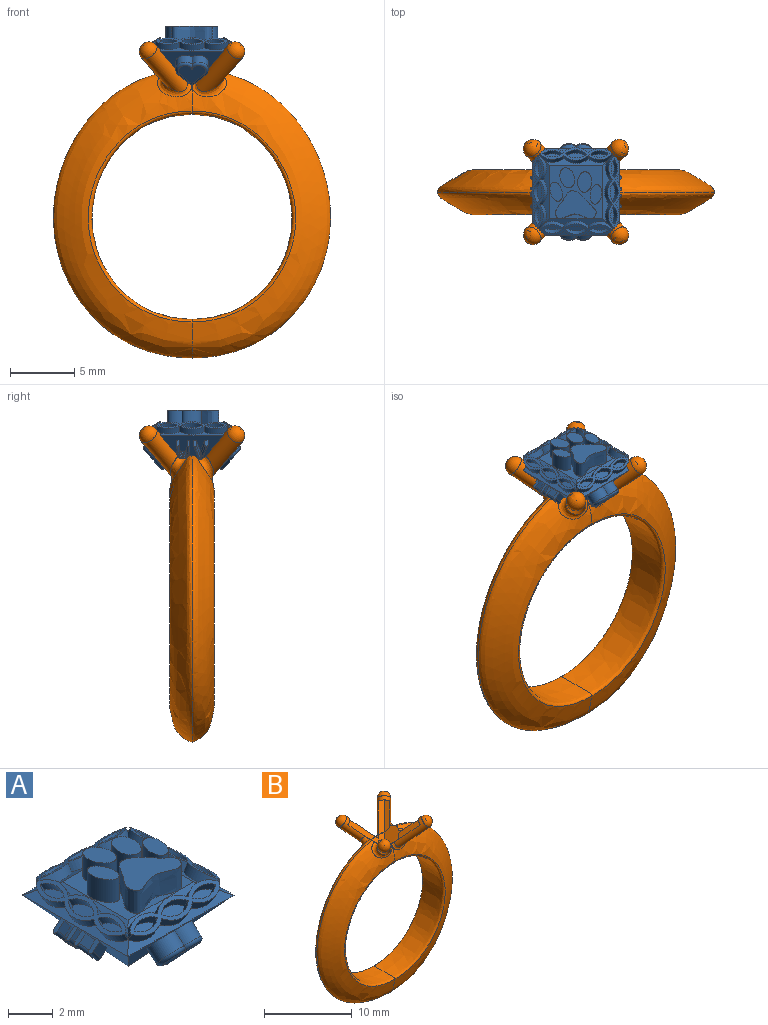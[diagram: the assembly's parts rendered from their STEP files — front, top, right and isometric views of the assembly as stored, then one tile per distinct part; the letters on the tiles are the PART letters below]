
ASSEMBLY  parts=2 mates=1
PART A: 238 faces, bbox 7.4x7.8x6 mm
  f0: plane 6.71x3.89mm, normal (0.76,0,-0.65), area 16mm2, adj f1,f54,f57,f114,f115,f116,f117,f118
  f1: plane 6.71x3.89mm, normal (0,-0.76,-0.65), area 13.2mm2, adj f0,f37,f52,f104,f105,f106,f107
  f2: plane 2.31x0.42mm, normal (0,0,1), area 0.5mm2, adj f35,f94
  f3: plane 4.19x4.17mm, normal (0,0,1), area 7.6mm2, adj f5,f16,f35,f51,f94,f96,f98,f100
  f4: cylinder r=0.1mm len=0.48mm, axis (0.5,0,-0.87), area 0mm2, adj f8,f9,f22,f65,f89
  f5: plane 4.83x0.53mm, normal (-0.5,0,0.87), area 1.4mm2, adj f3,f10,f12,f16,f35,f89,f90
  f6: plane 1.49x0.5mm, normal (-0.5,0,0.87), area 0.6mm2, adj f23,f87
  f7: plane 6.71x0.57mm, normal (-0.5,0,0.87), area 2.3mm2, adj f9,f11,f18,f37,f48,f52,f92
  f8: cylinder r=0.1mm len=0.47mm, axis (0,-0.5,-0.87), area 0mm2, adj f4,f14,f22,f63,f89
  f9: cylinder r=1.3mm len=1.84mm, axis (0.5,0,-0.87), area 1mm2, adj f4,f7,f22,f48,f65,f92
  f10: cylinder r=1.3mm len=1.91mm, axis (0.5,0,-0.87), area 1.1mm2, adj f5,f65,f89,f90
  f11: cylinder r=1.3mm len=1.84mm, axis (0.5,0,-0.87), area 1mm2, adj f7,f40,f41,f42,f46,f65,f92
  f12: plane 0.02x0.02mm, normal (0,0.5,-0.87), area 0mm2, adj f5,f13,f90
  f13: cylinder r=1.3mm len=1.84mm, axis (0,0.5,-0.87), area 0.9mm2, adj f12,f35,f40,f42,f43,f70,f90
  f14: cylinder r=1.3mm len=1.84mm, axis (0,-0.5,-0.87), area 0.9mm2, adj f8,f16,f21,f63,f88,f89
  f15: cylinder r=0.1mm len=0.48mm, axis (0,-0.5,-0.87), area 0mm2, adj f19,f20,f31,f63,f83
  f16: plane 4.83x0.53mm, normal (0,0.5,0.87), area 1.4mm2, adj f3,f5,f14,f21,f51,f83,f88
  f17: plane 1.49x0.5mm, normal (0,0.5,0.87), area 0.6mm2, adj f32,f81
  f18: plane 6.71x0.57mm, normal (0,0.5,0.87), area 2.3mm2, adj f7,f20,f22,f50,f54,f57,f85
  f19: cylinder r=0.1mm len=0.47mm, axis (-0.5,0,-0.87), area 0mm2, adj f15,f24,f31,f60,f83
  f20: cylinder r=1.3mm len=1.84mm, axis (0,-0.5,-0.87), area 1mm2, adj f15,f18,f31,f50,f63,f85
  f21: cylinder r=1.3mm len=1.91mm, axis (0,-0.5,-0.87), area 1.1mm2, adj f14,f16,f63,f83
  f22: cylinder r=1.3mm len=1.84mm, axis (0,-0.5,-0.87), area 1mm2, adj f4,f8,f9,f18,f48,f63,f85
  f23: cylinder r=1.1mm len=1.49mm, axis (0.5,0,-0.87), area 0.8mm2, adj f6,f65,f87
  f24: cylinder r=1.3mm len=1.84mm, axis (-0.5,0,-0.87), area 0.9mm2, adj f19,f30,f51,f60,f82,f83
  f25: cylinder r=0.1mm len=0.48mm, axis (-0.5,0,-0.87), area 0mm2, adj f26,f33,f44,f60,f77
  f26: cylinder r=1.3mm len=1.84mm, axis (-0.5,0,-0.87), area 1mm2, adj f25,f44,f54,f60,f66,f79
  f27: plane 1.49x0.5mm, normal (0.5,0,0.87), area 0.6mm2, adj f38,f75
  f28: plane 1.49x0.5mm, normal (0.5,0,0.87), area 0.6mm2, adj f58,f78
  f29: plane 1.64x0.63mm, normal (0.5,0,0.87), area 0.8mm2, adj f59,f80
  f30: cylinder r=1.3mm len=1.91mm, axis (-0.5,0,-0.87), area 1.1mm2, adj f24,f51,f60,f77
  f31: cylinder r=1.3mm len=1.84mm, axis (-0.5,0,-0.87), area 1mm2, adj f15,f19,f20,f50,f54,f60,f79
  f32: cylinder r=1.1mm len=1.49mm, axis (0,-0.5,-0.87), area 0.8mm2, adj f17,f63,f81
  f33: cylinder r=0.1mm len=0.47mm, axis (0,0.5,-0.87), area 0mm2, adj f25,f34,f44,f70,f77
  f34: cylinder r=1.3mm len=1.84mm, axis (0,0.5,-0.87), area 0.9mm2, adj f33,f35,f43,f70,f76,f77
  f35: plane 4.84x0.54mm, normal (0,-0.5,0.87), area 1.4mm2, adj f2,f3,f5,f13,f34,f43,f51,f76
  f36: plane 1.49x0.5mm, normal (0,-0.5,0.87), area 0.6mm2, adj f68,f74
  f37: plane 6.71x0.57mm, normal (0,-0.5,0.87), area 2.3mm2, adj f1,f7,f41,f44,f46,f54,f72
  f38: cylinder r=1.1mm len=1.49mm, axis (-0.5,0,-0.87), area 0.8mm2, adj f27,f60,f75
  f39: cylinder r=1.1mm len=1.49mm, axis (0.5,0,-0.87), area 0.8mm2, adj f47,f65,f91
  f40: cylinder r=0.1mm len=0.47mm, axis (0.5,0,-0.87), area 0mm2, adj f11,f13,f42,f65,f90
  f41: cylinder r=1.3mm len=1.84mm, axis (0,0.5,-0.87), area 1mm2, adj f11,f37,f42,f46,f70,f72
  f42: cylinder r=0.1mm len=0.48mm, axis (0,0.5,-0.87), area 0mm2, adj f11,f13,f40,f41,f70
  f43: cylinder r=1.3mm len=1.91mm, axis (0,0.5,-0.87), area 1.1mm2, adj f13,f34,f35,f70
  f44: cylinder r=1.3mm len=1.84mm, axis (0,0.5,-0.87), area 1mm2, adj f25,f26,f33,f37,f66,f70,f72
  f45: plane 1.49x0.5mm, normal (0,-0.5,0.87), area 0.6mm2, adj f67,f71
  f46: plane 0x0mm, normal (0.5,0,-0.87), area 0mm2, adj f11,f37,f41
  f47: plane 1.49x0.5mm, normal (-0.5,0,0.87), area 0.6mm2, adj f39,f91
  f48: plane 0x0mm, normal (0,-0.5,-0.87), area 0mm2, adj f7,f9,f22
  f49: plane 1.49x0.5mm, normal (0,0.5,0.87), area 0.6mm2, adj f61,f84
  f50: plane 0x0mm, normal (-0.5,0,-0.87), area 0mm2, adj f18,f20,f31
  f51: plane 4.83x0.53mm, normal (0.5,0,0.87), area 1.4mm2, adj f3,f16,f24,f30,f35,f77,f82
  f52: plane 6.71x3.89mm, normal (-0.76,0,-0.65), area 16mm2, adj f1,f7,f57,f148,f149,f150,f151,f152
  f53: plane 1.64x0.63mm, normal (-0.5,0,0.87), area 0.8mm2, adj f64,f93
  f54: plane 6.71x0.57mm, normal (0.5,0,0.87), area 2.3mm2, adj f0,f18,f26,f31,f37,f66,f79
  f55: plane 1.64x0.63mm, normal (0,0.5,0.87), area 0.8mm2, adj f62,f86
  f56: plane 1.64x0.63mm, normal (0,-0.5,0.87), area 0.8mm2, adj f69,f73
  f57: plane 6.71x3.89mm, normal (0,0.76,-0.65), area 13.2mm2, adj f0,f18,f52,f109,f110,f111,f112
  f58: cylinder r=1.1mm len=1.49mm, axis (-0.5,0,-0.87), area 0.8mm2, adj f28,f60,f78
  f59: cylinder r=1.1mm len=1.64mm, axis (-0.5,0,-0.87), area 0.9mm2, adj f29,f60,f80
  f60: plane 5.64x0.98mm, normal (0.5,0,0.87), area 2.4mm2, adj f19,f24,f25,f26,f30,f31,f38,f58
  f61: cylinder r=1.1mm len=1.49mm, axis (0,-0.5,-0.87), area 0.8mm2, adj f49,f63,f84
  f62: cylinder r=1.1mm len=1.64mm, axis (0,-0.5,-0.87), area 0.9mm2, adj f55,f63,f86
  f63: plane 5.64x0.98mm, normal (0,0.5,0.87), area 2.4mm2, adj f8,f14,f15,f20,f21,f22,f32,f61
  f64: cylinder r=1.1mm len=1.64mm, axis (0.5,0,-0.87), area 0.9mm2, adj f53,f65,f93
  f65: plane 5.64x0.98mm, normal (-0.5,0,0.87), area 2.4mm2, adj f4,f9,f10,f11,f23,f39,f40,f64
  f66: plane 0x0mm, normal (0,0.5,-0.87), area 0mm2, adj f26,f44,f54
  f67: cylinder r=1.1mm len=1.49mm, axis (0,0.5,-0.87), area 0.8mm2, adj f45,f70,f71
  f68: cylinder r=1.1mm len=1.49mm, axis (0,0.5,-0.87), area 0.8mm2, adj f36,f70,f74
  f69: cylinder r=1.1mm len=1.64mm, axis (0,0.5,-0.87), area 0.9mm2, adj f56,f70,f73
  f70: plane 5.64x0.98mm, normal (0,-0.5,0.87), area 2.4mm2, adj f13,f33,f34,f41,f42,f43,f44,f67
  f71: cylinder r=1.1mm len=1.49mm, axis (0,0.5,-0.87), area 0.8mm2, adj f45,f67,f70
  f72: cylinder r=1.3mm len=1.91mm, axis (0,0.5,-0.87), area 1.1mm2, adj f37,f41,f44,f70
  f73: cylinder r=1.1mm len=1.64mm, axis (0,0.5,-0.87), area 0.9mm2, adj f56,f69,f70
  f74: cylinder r=1.1mm len=1.49mm, axis (0,0.5,-0.87), area 0.8mm2, adj f36,f68,f70
  f75: cylinder r=1.1mm len=1.49mm, axis (-0.5,0,-0.87), area 0.8mm2, adj f27,f38,f60
  f76: plane 0.02x0.02mm, normal (-0.5,0,-0.87), area 0mm2, adj f34,f35,f77
  f77: cylinder r=1.3mm len=1.84mm, axis (-0.5,0,-0.87), area 0.9mm2, adj f25,f30,f33,f34,f51,f60,f76
  f78: cylinder r=1.1mm len=1.49mm, axis (-0.5,0,-0.87), area 0.8mm2, adj f28,f58,f60
  f79: cylinder r=1.3mm len=1.91mm, axis (-0.5,0,-0.87), area 1.1mm2, adj f26,f31,f54,f60
  f80: cylinder r=1.1mm len=1.64mm, axis (-0.5,0,-0.87), area 0.9mm2, adj f29,f59,f60
  f81: cylinder r=1.1mm len=1.49mm, axis (0,-0.5,-0.87), area 0.8mm2, adj f17,f32,f63
  f82: plane 0.02x0.02mm, normal (0,-0.5,-0.87), area 0mm2, adj f24,f51,f83
  f83: cylinder r=1.3mm len=1.84mm, axis (0,-0.5,-0.87), area 0.9mm2, adj f15,f16,f19,f21,f24,f63,f82
  f84: cylinder r=1.1mm len=1.49mm, axis (0,-0.5,-0.87), area 0.8mm2, adj f49,f61,f63
  f85: cylinder r=1.3mm len=1.91mm, axis (0,-0.5,-0.87), area 1.1mm2, adj f18,f20,f22,f63
  f86: cylinder r=1.1mm len=1.64mm, axis (0,-0.5,-0.87), area 0.9mm2, adj f55,f62,f63
  f87: cylinder r=1.1mm len=1.49mm, axis (0.5,0,-0.87), area 0.8mm2, adj f6,f23,f65
  f88: plane 0.02x0.02mm, normal (0.5,0,-0.87), area 0mm2, adj f14,f16,f89
  f89: cylinder r=1.3mm len=1.84mm, axis (0.5,0,-0.87), area 0.9mm2, adj f4,f5,f8,f10,f14,f65,f88
  f90: cylinder r=1.3mm len=1.84mm, axis (0.5,0,-0.87), area 0.9mm2, adj f5,f10,f12,f13,f40,f65
  f91: cylinder r=1.1mm len=1.49mm, axis (0.5,0,-0.87), area 0.8mm2, adj f39,f47,f65
  f92: cylinder r=1.3mm len=1.91mm, axis (0.5,0,-0.87), area 1.1mm2, adj f7,f9,f11,f65
  f93: cylinder r=1.1mm len=1.64mm, axis (0.5,0,-0.87), area 0.9mm2, adj f53,f64,f65
  f94: extruded ~3.14x2.18mm, area 11mm2, adj f2,f3,f35,f95
  f95: plane 3.24x2.27mm, normal (0,0,1), area 4.3mm2, adj f94
  f96: extruded ~1.49x1.25mm, area 4.9mm2, adj f3,f97
  f97: plane 1.49x0.98mm, normal (0,0,1), area 1.1mm2, adj f96
  f98: extruded ~1.52x1.25mm, area 4.9mm2, adj f3,f99
  f99: plane 1.52x0.92mm, normal (0,0,1), area 1.1mm2, adj f98
  f100: extruded ~1.56x1.25mm, area 5.3mm2, adj f3,f101
  f101: plane 1.56x1.15mm, normal (0,0,1), area 1.4mm2, adj f100
  f102: extruded ~1.59x1.25mm, area 5.3mm2, adj f3,f103
  f103: plane 1.6x1.1mm, normal (0,0,1), area 1.4mm2, adj f102
  f104: cylinder r=0.75mm len=1.49mm, axis (0,0.76,0.65), area 1.9mm2, adj f1,f105,f107,f234
  f105: plane 1.33x1.3mm, normal (-0.71,0.46,-0.54), area 1.2mm2, adj f1,f104,f106,f236
  f106: plane 1.33x1.3mm, normal (0.71,0.46,-0.54), area 1.2mm2, adj f1,f105,f107,f237
  f107: cylinder r=0.75mm len=1.49mm, axis (0,0.76,0.65), area 1.9mm2, adj f1,f104,f106,f235
  f108: plane 2.16x1.41mm, normal (0,-0.76,-0.65), area 2.6mm2, adj f234,f235,f236,f237
  f109: cylinder r=0.75mm len=1.49mm, axis (0,-0.76,0.65), area 1.9mm2, adj f57,f110,f112,f230
  f110: plane 1.33x1.3mm, normal (0.71,-0.46,-0.54), area 1.2mm2, adj f57,f109,f111,f232
  f111: plane 1.33x1.3mm, normal (-0.71,-0.46,-0.54), area 1.2mm2, adj f57,f110,f112,f233
  f112: cylinder r=0.75mm len=1.49mm, axis (0,-0.76,0.65), area 1.9mm2, adj f57,f109,f111,f231
  f113: plane 2.16x1.41mm, normal (0,0.76,-0.65), area 2.6mm2, adj f230,f231,f232,f233
  f114: extruded ~0.57x0.54mm, area 0.1mm2, adj f0,f115,f125,f215
  f115: plane 0.85x0.84mm, normal (0,1,0), area 0.4mm2, adj f0,f114,f116,f213
  f116: plane 0.55x0.48mm, normal (0.65,0,0.76), area 0.2mm2, adj f0,f115,f117,f212,f213
  f117: plane 0.87x0.86mm, normal (0,-1,0), area 0.4mm2, adj f0,f116,f118,f212
  f118: extruded ~0.61x0.58mm, area 0.2mm2, adj f0,f117,f119,f214
  f119: extruded ~0.56x0.52mm, area 0.1mm2, adj f0,f118,f120,f216
  f120: extruded ~0.5x0.46mm, area 0.1mm2, adj f0,f119,f121,f219
  f121: extruded ~0.45x0.4mm, area 0.1mm2, adj f0,f120,f122,f218
  f122: plane 0.65x0.59mm, normal (0,1,0), area 0.1mm2, adj f0,f121,f123,f218,f221
  f123: extruded ~0.44x0.39mm, area 0.1mm2, adj f0,f122,f124,f221
  f124: extruded ~0.48x0.43mm, area 0.1mm2, adj f0,f123,f125,f220
  f125: extruded ~0.52x0.48mm, area 0.1mm2, adj f0,f114,f124,f217
  f126: plane 0.87x0.86mm, normal (0,1,0), area 0.4mm2, adj f0,f127,f137,f203
  f127: plane 0.55x0.48mm, normal (0.65,0,0.76), area 0.2mm2, adj f0,f126,f128,f202,f203
  f128: plane 0.85x0.84mm, normal (0,-1,0), area 0.4mm2, adj f0,f127,f129,f202
  f129: extruded ~0.58x0.54mm, area 0.1mm2, adj f0,f128,f130,f204
  f130: extruded ~0.52x0.48mm, area 0.1mm2, adj f0,f129,f131,f206
  f131: extruded ~0.48x0.43mm, area 0.1mm2, adj f0,f130,f132,f208
  f132: extruded ~0.44x0.39mm, area 0.1mm2, adj f0,f131,f133,f211
  f133: plane 0.69x0.63mm, normal (0,-1,0), area 0.1mm2, adj f0,f132,f134,f210,f211
  f134: extruded ~0.45x0.4mm, area 0.1mm2, adj f0,f133,f135,f210
  f135: extruded ~0.5x0.46mm, area 0.1mm2, adj f0,f134,f136,f209
  f136: extruded ~0.56x0.52mm, area 0.1mm2, adj f0,f135,f137,f207
  f137: extruded ~0.61x0.58mm, area 0.2mm2, adj f0,f126,f136,f205
  f138: plane 0.57x0.5mm, normal (0.65,0,0.76), area 0.2mm2, adj f0,f139,f142,f228,f229
  f139: plane 1.39x1.31mm, normal (-0.19,-0.96,-0.22), area 0.8mm2, adj f0,f138,f140,f229
  f140: plane 0.56x0.48mm, normal (-0.65,0,-0.76), area 0.1mm2, adj f0,f139,f141,f228,f229
  f141: plane 0.69x0.64mm, normal (0,1,0), area 0.2mm2, adj f0,f140,f142,f228
  f142: plane 1.17x1.11mm, normal (0.17,0.97,0.2), area 0.6mm2, adj f0,f138,f141,f228
  f143: plane 0.57x0.49mm, normal (0.65,0,0.76), area 0.2mm2, adj f0,f144,f147,f226,f227
  f144: plane 1.12x1.07mm, normal (0.18,-0.96,0.21), area 0.6mm2, adj f0,f143,f145,f227
  f145: plane 0.9x0.83mm, normal (0,-1,0), area 0.2mm2, adj f0,f144,f146,f226,f227
  f146: plane 0.54x0.47mm, normal (-0.65,0,-0.76), area 0.1mm2, adj f0,f145,f147,f226
  f147: plane 1.39x1.31mm, normal (-0.2,0.95,-0.23), area 0.8mm2, adj f0,f143,f146,f226
  f148: extruded ~0.57x0.54mm, area 0.1mm2, adj f52,f149,f159,f195
  f149: plane 0.85x0.84mm, normal (0,-1,0), area 0.4mm2, adj f52,f148,f150,f193
  f150: plane 0.55x0.48mm, normal (-0.65,0,0.76), area 0.2mm2, adj f52,f149,f151,f192,f193
  f151: plane 0.87x0.86mm, normal (0,1,0), area 0.4mm2, adj f52,f150,f152,f192
  f152: extruded ~0.61x0.58mm, area 0.2mm2, adj f52,f151,f153,f194
  f153: extruded ~0.56x0.52mm, area 0.1mm2, adj f52,f152,f154,f196
  f154: extruded ~0.5x0.46mm, area 0.1mm2, adj f52,f153,f155,f199
  f155: extruded ~0.45x0.4mm, area 0.1mm2, adj f52,f154,f156,f198
  f156: plane 0.65x0.59mm, normal (0,-1,0), area 0.1mm2, adj f52,f155,f157,f198,f201
  f157: extruded ~0.44x0.39mm, area 0.1mm2, adj f52,f156,f158,f201
  f158: extruded ~0.48x0.43mm, area 0.1mm2, adj f52,f157,f159,f200
  f159: extruded ~0.52x0.48mm, area 0.1mm2, adj f52,f148,f158,f197
  f160: plane 0.87x0.86mm, normal (0,-1,0), area 0.4mm2, adj f52,f161,f171,f183
  f161: plane 0.55x0.48mm, normal (-0.65,0,0.76), area 0.2mm2, adj f52,f160,f162,f182,f183
  f162: plane 0.85x0.84mm, normal (0,1,0), area 0.4mm2, adj f52,f161,f163,f182
  f163: extruded ~0.58x0.54mm, area 0.1mm2, adj f52,f162,f164,f184
  f164: extruded ~0.52x0.48mm, area 0.1mm2, adj f52,f163,f165,f186
  f165: extruded ~0.48x0.43mm, area 0.1mm2, adj f52,f164,f166,f188
  f166: extruded ~0.44x0.39mm, area 0.1mm2, adj f52,f165,f167,f191
  f167: plane 0.69x0.63mm, normal (0,1,0), area 0.1mm2, adj f52,f166,f168,f190,f191
  f168: extruded ~0.45x0.4mm, area 0.1mm2, adj f52,f167,f169,f190
  f169: extruded ~0.5x0.46mm, area 0.1mm2, adj f52,f168,f170,f189
  f170: extruded ~0.56x0.52mm, area 0.1mm2, adj f52,f169,f171,f187
  f171: extruded ~0.61x0.58mm, area 0.2mm2, adj f52,f160,f170,f185
  f172: plane 0.57x0.5mm, normal (-0.65,0,0.76), area 0.2mm2, adj f52,f173,f176,f224,f225
  f173: plane 1.39x1.31mm, normal (0.19,0.96,-0.22), area 0.8mm2, adj f52,f172,f174,f225
  f174: plane 0.56x0.48mm, normal (0.65,0,-0.76), area 0.1mm2, adj f52,f173,f175,f224,f225
  f175: plane 0.69x0.64mm, normal (0,-1,0), area 0.2mm2, adj f52,f174,f176,f224
  f176: plane 1.17x1.11mm, normal (-0.17,-0.97,0.2), area 0.6mm2, adj f52,f172,f175,f224
  f177: plane 0.57x0.49mm, normal (-0.65,0,0.76), area 0.2mm2, adj f52,f178,f181,f222,f223
  f178: plane 1.12x1.07mm, normal (-0.18,0.96,0.21), area 0.6mm2, adj f52,f177,f179,f223
  f179: plane 0.9x0.83mm, normal (0,1,0), area 0.2mm2, adj f52,f178,f180,f222,f223
  f180: plane 0.54x0.47mm, normal (0.65,0,-0.76), area 0.1mm2, adj f52,f179,f181,f222
  f181: plane 1.39x1.31mm, normal (0.2,-0.95,-0.23), area 0.8mm2, adj f52,f177,f180,f222
  f182: cylinder r=0.2mm len=0.61mm, axis (-0.65,0,0.76), area 0.1mm2, adj f161,f162,f183,f184
  f183: cylinder r=0.2mm len=0.63mm, axis (0.65,0,-0.76), area 0.1mm2, adj f160,f161,f182,f184,f185
  f184: bspline ~0.39x0.35mm, area 0.1mm2, adj f163,f182,f183,f185,f186
  f185: bspline ~0.45x0.43mm, area 0.1mm2, adj f171,f183,f184,f186,f187
  f186: bspline ~0.36x0.29mm, area 0mm2, adj f164,f184,f185,f187,f188
  f187: bspline ~0.39x0.37mm, area 0mm2, adj f170,f185,f186,f188,f189
  f188: bspline ~0.34x0.28mm, area 0mm2, adj f165,f186,f187,f189,f191
  f189: bspline ~0.35x0.3mm, area 0mm2, adj f169,f187,f188,f190,f191
  f190: bspline ~0.31x0.26mm, area 0mm2, adj f167,f168,f189,f191
  f191: bspline ~0.33x0.28mm, area 0mm2, adj f166,f167,f188,f189,f190
  f192: cylinder r=0.2mm len=0.63mm, axis (-0.65,0,0.76), area 0.2mm2, adj f150,f151,f193,f194,f195
  f193: cylinder r=0.2mm len=0.61mm, axis (0.65,0,-0.76), area 0.1mm2, adj f149,f150,f192,f195
  f194: bspline ~0.45x0.43mm, area 0.1mm2, adj f152,f192,f195,f196,f197
  f195: bspline ~0.42x0.38mm, area 0.1mm2, adj f148,f192,f193,f194,f197
  f196: bspline ~0.39x0.37mm, area 0mm2, adj f153,f194,f197,f199,f200
  f197: bspline ~0.37x0.29mm, area 0mm2, adj f159,f194,f195,f196,f200
  f198: bspline ~0.32x0.27mm, area 0mm2, adj f155,f156,f199,f201
  f199: bspline ~0.35x0.3mm, area 0mm2, adj f154,f196,f198,f200,f201
  f200: bspline ~0.36x0.28mm, area 0mm2, adj f158,f196,f197,f199,f201
  f201: bspline ~0.45x0.36mm, area 0mm2, adj f156,f157,f198,f199,f200
  f202: cylinder r=0.2mm len=0.61mm, axis (0.65,0,0.76), area 0.1mm2, adj f127,f128,f203,f204
  f203: cylinder r=0.2mm len=0.63mm, axis (-0.65,0,-0.76), area 0.1mm2, adj f126,f127,f202,f204,f205
  f204: bspline ~0.39x0.35mm, area 0.1mm2, adj f129,f202,f203,f205,f206
  f205: bspline ~0.45x0.43mm, area 0.1mm2, adj f137,f203,f204,f206,f207
  f206: bspline ~0.36x0.29mm, area 0mm2, adj f130,f204,f205,f207,f208
  f207: bspline ~0.39x0.37mm, area 0mm2, adj f136,f205,f206,f208,f209
  f208: bspline ~0.34x0.28mm, area 0mm2, adj f131,f206,f207,f209,f211
  f209: bspline ~0.35x0.3mm, area 0mm2, adj f135,f207,f208,f210,f211
  f210: bspline ~0.31x0.26mm, area 0mm2, adj f133,f134,f209,f211
  f211: bspline ~0.33x0.28mm, area 0mm2, adj f132,f133,f208,f209,f210
  f212: cylinder r=0.2mm len=0.63mm, axis (0.65,0,0.76), area 0.2mm2, adj f116,f117,f213,f214,f215
  f213: cylinder r=0.2mm len=0.61mm, axis (-0.65,0,-0.76), area 0.1mm2, adj f115,f116,f212,f215
  f214: bspline ~0.45x0.43mm, area 0.1mm2, adj f118,f212,f215,f216,f217
  f215: bspline ~0.42x0.38mm, area 0.1mm2, adj f114,f212,f213,f214,f217
  f216: bspline ~0.39x0.37mm, area 0mm2, adj f119,f214,f217,f219,f220
  f217: bspline ~0.37x0.29mm, area 0mm2, adj f125,f214,f215,f216,f220
  f218: bspline ~0.32x0.27mm, area 0mm2, adj f121,f122,f219,f221
  f219: bspline ~0.35x0.3mm, area 0mm2, adj f120,f216,f218,f220,f221
  f220: bspline ~0.36x0.28mm, area 0mm2, adj f124,f216,f217,f219,f221
  f221: bspline ~0.45x0.36mm, area 0mm2, adj f122,f123,f218,f219,f220
  f222: cylinder r=0.2mm len=1.15mm, axis (0.62,0.31,-0.72), area 0.3mm2, adj f177,f179,f180,f181,f223
  f223: cylinder r=0.2mm len=1.18mm, axis (-0.63,-0.27,0.73), area 0.3mm2, adj f177,f178,f179,f222
  f224: cylinder r=0.2mm len=1.19mm, axis (0.63,-0.26,-0.73), area 0.3mm2, adj f172,f174,f175,f176,f225
  f225: cylinder r=0.2mm len=1.15mm, axis (-0.62,0.3,0.72), area 0.3mm2, adj f172,f173,f174,f224
  f226: cylinder r=0.2mm len=1.15mm, axis (-0.62,-0.31,-0.72), area 0.3mm2, adj f143,f145,f146,f147,f227
  f227: cylinder r=0.2mm len=1.18mm, axis (0.63,0.27,0.73), area 0.3mm2, adj f143,f144,f145,f226
  f228: cylinder r=0.2mm len=1.19mm, axis (-0.63,0.26,-0.73), area 0.3mm2, adj f138,f140,f141,f142,f229
  f229: cylinder r=0.2mm len=1.15mm, axis (0.62,-0.3,0.72), area 0.3mm2, adj f138,f139,f140,f228
  f230: torus R=0.55mm, axis (0,0.76,-0.65), area 0.7mm2, adj f109,f113,f231,f232
  f231: torus R=0.55mm, axis (0,0.76,-0.65), area 0.7mm2, adj f112,f113,f230,f233
  f232: cylinder r=0.2mm len=1.2mm, axis (0.71,0.46,0.54), area 0.4mm2, adj f110,f113,f230,f233
  f233: cylinder r=0.2mm len=1.2mm, axis (0.71,-0.46,-0.54), area 0.4mm2, adj f111,f113,f231,f232
  f234: torus R=0.55mm, axis (0,-0.76,-0.65), area 0.7mm2, adj f104,f108,f235,f236
  f235: torus R=0.55mm, axis (0,-0.76,-0.65), area 0.7mm2, adj f107,f108,f234,f237
  f236: cylinder r=0.2mm len=1.2mm, axis (-0.71,-0.46,0.54), area 0.4mm2, adj f105,f108,f234,f237
  f237: cylinder r=0.2mm len=1.2mm, axis (-0.71,0.46,-0.54), area 0.4mm2, adj f106,f108,f235,f236
PART B: 50 faces, bbox 30.5x8.8x25.2 mm
  f0: plane 0.26x0.23mm, normal (0.76,0,-0.65), area 0mm2, adj f1,f3,f4
  f1: plane 0.26x0.23mm, normal (-0.76,0,-0.65), area 0mm2, adj f0,f2,f4
  f2: cylinder r=0.75mm len=1.15mm, axis (-0.55,0.55,0.63), area 0.3mm2, adj f1,f3,f4,f5
  f3: cylinder r=0.75mm len=1.15mm, axis (0.55,0.55,0.63), area 0.3mm2, adj f0,f2,f4,f5
  f4: plane 1.4x0.7mm, normal (0,1,0), area 0.2mm2, adj f0,f1,f2,f3,f5
  f5: plane 0.32x0.19mm, normal (0,-0.76,0.65), area 0mm2, adj f2,f3,f4
  f6: plane 0.26x0.23mm, normal (-0.76,0,-0.65), area 0mm2, adj f7,f9,f10
  f7: plane 0.26x0.23mm, normal (0.76,0,-0.65), area 0mm2, adj f6,f8,f10
  f8: cylinder r=0.75mm len=1.15mm, axis (0.55,-0.55,0.63), area 0.3mm2, adj f7,f9,f10,f11
  f9: cylinder r=0.75mm len=1.15mm, axis (-0.55,-0.55,0.63), area 0.3mm2, adj f6,f8,f10,f11
  f10: plane 1.4x0.7mm, normal (0,-1,0), area 0.2mm2, adj f6,f7,f8,f9,f11
  f11: plane 0.32x0.19mm, normal (0,0.76,0.65), area 0mm2, adj f8,f9,f10
  f12: plane 2.78x2.71mm, normal (-0.76,0,0.65), area 4mm2, adj f16,f17,f22,f27,f28,f31,f34,f39
  f13: plane 2.63x2.23mm, normal (0.76,0,0.65), area 2.5mm2, adj f14,f15,f22,f23,f26,f36,f37,f40
  f14: bspline ~22.51x14.98mm, area 102mm2, adj f13,f15,f16,f18,f20,f35,f40
  f15: bspline ~22.51x14.98mm, area 102mm2, adj f13,f14,f17,f18,f21,f25,f26
  f16: bspline ~22.51x14.98mm, area 102mm2, adj f12,f14,f17,f19,f20,f32,f41
  f17: bspline ~22.51x14.98mm, area 102mm2, adj f12,f15,f16,f19,f21,f29,f39
  f18: bspline ~16.44x8.05mm, area 94.4mm2, adj f14,f15,f19
  f19: bspline ~16.44x8.05mm, area 94.4mm2, adj f16,f17,f18
  f20: plane 2.29x0.13mm, normal (0,-1,0), area 0.1mm2, adj f14,f16,f31,f38
  f21: plane 2.3x0.13mm, normal (0,1,0), area 0.1mm2, adj f15,f17,f22,f27
  f22: plane 1.61x1.33mm, normal (0,0.76,0.65), area 1.3mm2, adj f12,f13,f21,f27,f37
  f23: plane 3.22x3.15mm, normal (0.76,0,0.65), area 2.7mm2, adj f13,f24,f25,f43
  f24: cylinder r=0.75mm len=3.96mm, axis (-0.55,-0.55,0.63), area 12.4mm2, adj f23,f25,f26,f42,f43
  f25: plane 3.38x2.62mm, normal (0,0.76,0.65), area 3mm2, adj f15,f23,f24,f26,f43
  f26: bspline ~2.67x1.96mm, area 2.6mm2, adj f13,f15,f24,f25
  f27: plane 1.14x0.8mm, normal (0,0.76,0.65), area 0.6mm2, adj f12,f21,f22
  f28: plane 2.65x2.59mm, normal (-0.76,0,0.65), area 2.7mm2, adj f12,f29,f30,f48
  f29: plane 3.91x3.15mm, normal (0,0.76,0.65), area 3mm2, adj f17,f28,f30,f39,f48
  f30: cylinder r=0.75mm len=3.96mm, axis (0.55,-0.55,0.63), area 12.4mm2, adj f28,f29,f39,f48,f49
  f31: plane 1.59x1.32mm, normal (0,-0.76,0.65), area 1.3mm2, adj f12,f20,f37,f38
  f32: plane 3.38x2.62mm, normal (0,-0.76,0.65), area 3mm2, adj f16,f33,f34,f41,f46
  f33: cylinder r=0.75mm len=3.96mm, axis (0.55,0.55,0.63), area 12.4mm2, adj f32,f34,f41,f46,f47
  f34: plane 3.22x3.15mm, normal (-0.76,0,0.65), area 2.7mm2, adj f12,f32,f33,f46
  f35: plane 3.91x3.16mm, normal (0,-0.76,0.65), area 3mm2, adj f14,f36,f37,f40,f45
  f36: cylinder r=0.75mm len=3.96mm, axis (-0.55,0.55,0.63), area 12.4mm2, adj f13,f35,f37,f40,f44,f45
  f37: plane 3.89x3.81mm, normal (0.76,0,0.65), area 4.3mm2, adj f13,f22,f31,f35,f36,f38,f45
  f38: plane 1.13x0.79mm, normal (0,-0.76,0.65), area 0.6mm2, adj f20,f31,f37
  f39: bspline ~2.67x1.96mm, area 2.7mm2, adj f12,f17,f29,f30
  f40: bspline ~2.67x1.96mm, area 2.7mm2, adj f13,f14,f35,f36
  f41: bspline ~2.67x1.96mm, area 3.1mm2, adj f12,f16,f32,f33
  f42: sphere r=0.75mm, area 3.5mm2, adj f24
  f43: cone r=0mm half-angle=56.8deg, axis (0.55,0.55,-0.63), area 0.9mm2, adj f23,f24,f25
  f44: sphere r=0.75mm, area 3.5mm2, adj f36
  f45: cone r=0mm half-angle=56.8deg, axis (0.55,-0.55,-0.63), area 0.9mm2, adj f35,f36,f37
  f46: cone r=0mm half-angle=56.8deg, axis (-0.55,-0.55,-0.63), area 0.9mm2, adj f32,f33,f34
  f47: sphere r=0.75mm, area 3.5mm2, adj f33
  f48: cone r=0mm half-angle=56.8deg, axis (-0.55,0.55,-0.63), area 0.9mm2, adj f28,f29,f30
  f49: sphere r=0.75mm, area 3.5mm2, adj f30
PLACE A rot(axis=(-0.93,-0.36,0),0deg) t=(0,3.35,5.62)mm
PLACE B at identity fixed
MATE fastened A.f0 <-> B.f34  axis (0.76,0,-0.65) through (3.35,3.35,4.89)mm
